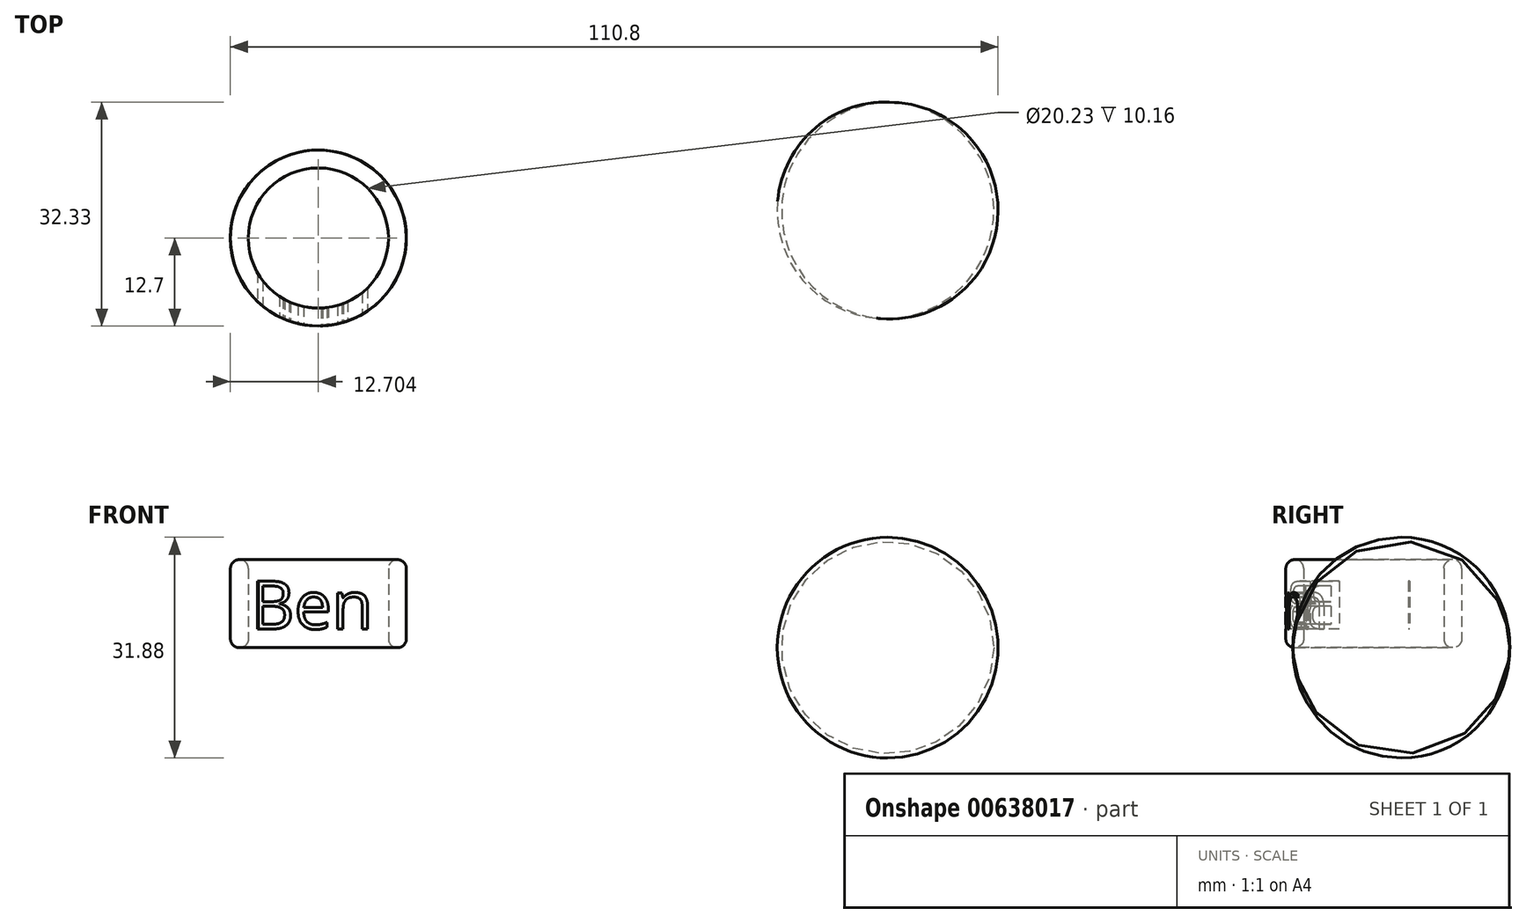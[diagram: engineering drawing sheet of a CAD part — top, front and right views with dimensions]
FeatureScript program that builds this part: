
annotation { "Feature Type Name" : "Feature", "Feature Type Description" : "" }
export const myFeature = defineFeature(function(context is Context, id is Id, definition is map)
    precondition{}
    {
        {
            var Q0;
            Q0=qCreatedBy(makeId("Top.planeOp"),FACE);
            var sketch = newSketch(context, id + "F0", { "sketchPlane" : qUnion([Q0])});
            skCircle(sketch, "E0", {"center": v(-45.89, 20.2) * mm, "radius": 12.7 * mm});
            skCircle(sketch, "E1", {"center": v(-45.89, 20.2) * mm, "radius": 10.11 * mm});
            skSolve(sketch);
        }
        {
            var Q0;
            Q0=makeQuery(id+"F0.imprint","IMPRINT",FACE,{"disambiguationData":[TD([[makeQuery(id+"F0.imprint","IMPRINT",EDGE,{"derivedFrom":sQuery(id+"F0.wireOp",EDGE,"E0")}),1.0]])]});
            extrude(context, id + "F1", {"entities" : qUnion([Q0]), "depth" : 12.7 * mm, "offsetDistance" : 25.4 * mm});
        }
        {
            var Q0;
            Q0=makeQuery(id+"F1.opExtrude","CAP_EDGE",EDGE,{"disambiguationData":[OSD([sQuery(id+"F0.wireOp",EDGE,"E1")])],"isStart":false});
            var Q1;
            Q1=makeQuery(id+"F1.opExtrude","CAP_EDGE",EDGE,{"disambiguationData":[OSD([sQuery(id+"F0.wireOp",EDGE,"E0")])],"isStart":false});
            var Q2;
            Q2=makeQuery(id+"F1.opExtrude","CAP_EDGE",EDGE,{"disambiguationData":[OSD([sQuery(id+"F0.wireOp",EDGE,"E0")])],"isStart":true});
            var Q3;
            Q3=makeQuery(id+"F1.opExtrude","CAP_EDGE",EDGE,{"disambiguationData":[OSD([sQuery(id+"F0.wireOp",EDGE,"E1")])],"isStart":true});
            fillet(context, id + "F2", {"entities" : qUnion([Q0, Q1, Q2, Q3]), "radius" : 1.27 * mm, "tangentPropagation" : true, "allowEdgeOverflow" : false});
        }
        {
            var Q0;
            Q0=qCreatedBy(makeId("Front.planeOp"),FACE);
            var sketch = newSketch(context, id + "F3", { "sketchPlane" : qUnion([Q0])});
            skText(sketch, "E2", { "text": "Ben", "fontName": "OpenSans-Regular.ttf"});
            const initialGuessF3  = {"E2": [-0.05563, 0.0027, 1, 0, 0.00696]};
            skSetInitialGuess(sketch, initialGuessF3);
            skSolve(sketch);
        }
        {
            var Q0;
            Q0 = qSketchRegion(id + "F3", true);
            extrude(context, id + "F4", {"entities" : qUnion([Q0]), "operationType" : NewBodyOperationType.REMOVE, "oppositeDirection" : true, "depth" : 25.4 * mm, "offsetDistance" : 25.4 * mm});
        }
        {
            var Q0;
            Q0=qCreatedBy(makeId("Top.planeOp"),FACE);
            var sketch = newSketch(context, id + "F5", { "sketchPlane" : qUnion([Q0])});
            skArc(sketch, "E3", {"start": v(37.6, 39.76) * mm, "mid": v(21, 25.48) * mm, "end": v(34.95, 8.61) * mm});
            skLineSegment(sketch, "E4", {"start": v(37.6, 39.76) * mm, "end": v(34.95, 8.61) * mm});
            skSolve(sketch);
        }
        {
            var Q0;
            Q0=makeQuery(id+"F5.imprint","IMPRINT",FACE,{"disambiguationData":[TD([[makeQuery(id+"F5.imprint","IMPRINT",EDGE,{"derivedFrom":sQuery(id+"F5.wireOp",EDGE,"E3")}),1.0]])]});
            var Q1;
            Q1=sQuery(id+"F5.wireOp",EDGE,"E4");
            revolve(context, id + "F6", {"entities" : qUnion([Q0]), "axis" : qUnion([Q1]), "revolveType" : RevolveType.FULL});
        }
    });
